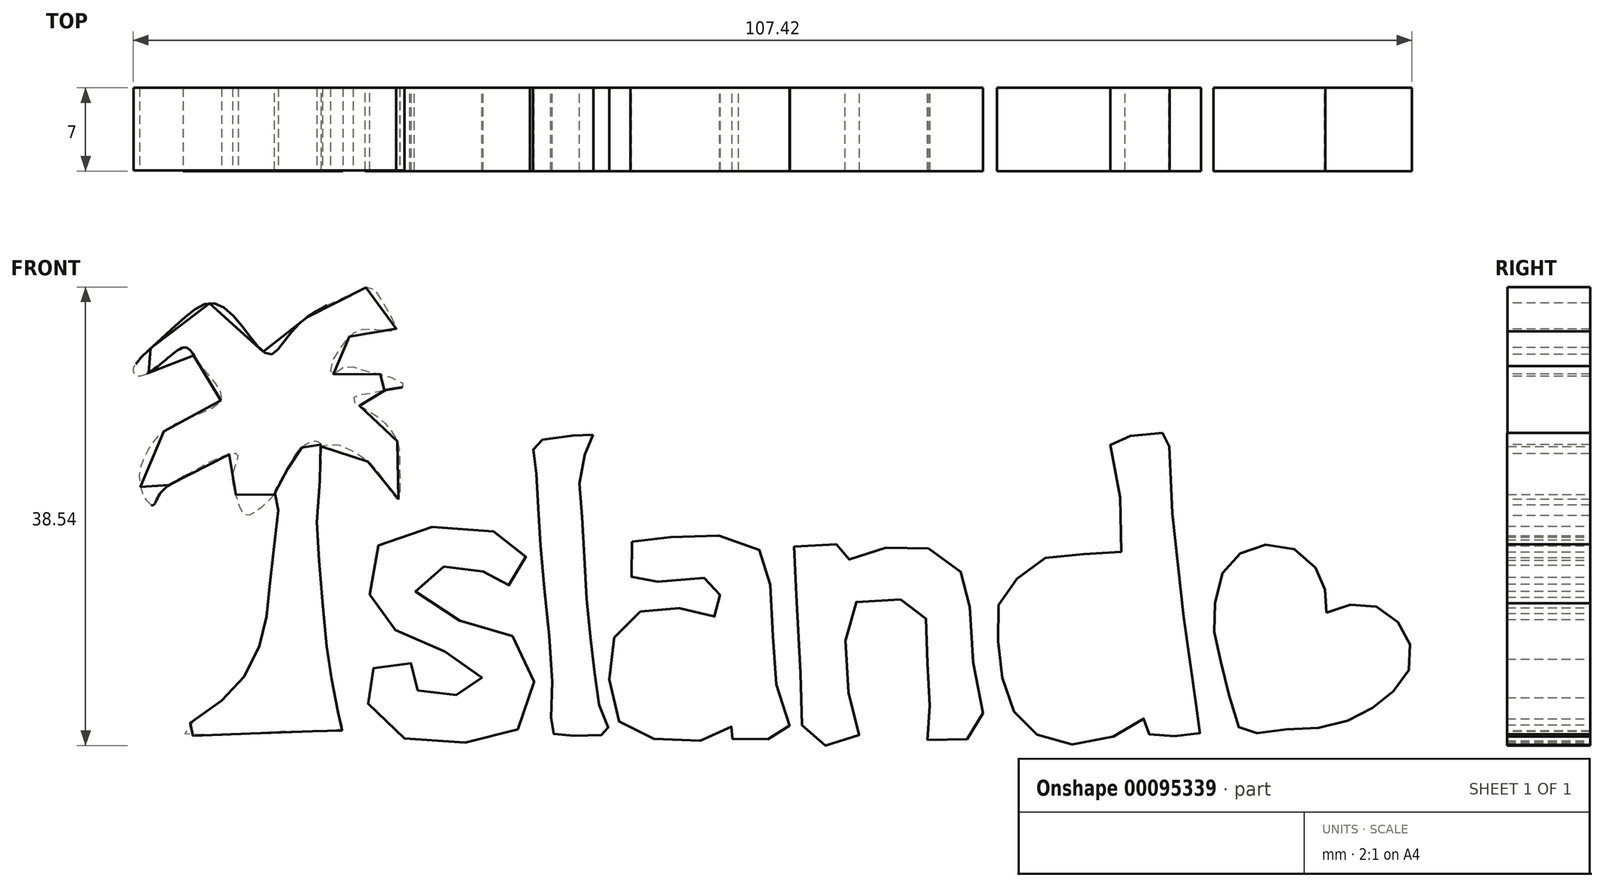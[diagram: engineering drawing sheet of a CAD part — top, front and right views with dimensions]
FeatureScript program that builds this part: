
annotation { "Feature Type Name" : "Feature", "Feature Type Description" : "" }
export const myFeature = defineFeature(function(context is Context, id is Id, definition is map)
    precondition{}
    {
        {
            var Q0;
            Q0=qCreatedBy(makeId("Front.planeOp"),FACE);
            var sketch = newSketch(context, id + "F0", { "sketchPlane" : qUnion([Q0])});
            skFitSpline(sketch, "E0", {"points": [v(-36.15, 19.95) * mm, v(-34.69, 20.39) * mm, v(-34.76, 16) * mm, v(-34.72, 10.92) * mm, v(-34.16, 4.35) * mm, v(-33.66, 0.5) * mm, v(-32.91, -2.96) * mm, v(-32.73, -3.8) * mm, v(-36.43, -3.89) * mm, v(-46.1, -4.03) * mm, v(-43.88, -2.08) * mm, v(-41.01, 0.65) * mm, v(-39.44, 4.16) * mm, v(-38.97, 6.94) * mm, v(-38.56, 11.06) * mm, v(-38.19, 15.4) * mm, v(-38.43, 16.02) * mm, v(-37.38, 18.07) * mm, v(-36.15, 19.95) * mm]});
            skFitSpline(sketch, "E1", {"points": [v(-26.39, -0.46) * mm, v(-26.94, 0) * mm, v(-27.04, 0.92) * mm, v(-27.04, 1.94) * mm, v(-28.24, 2.08) * mm, v(-30.23, 1.34) * mm, v(-30.7, 0.92) * mm, v(-30.74, -0.97) * mm, v(-29.4, -3.56) * mm, v(-26.94, -4.63) * mm, v(-23.1, -4.86) * mm, v(-19.3, -4.54) * mm, v(-17.6, -3.2) * mm, v(-16.72, -0.46) * mm, v(-16.76, 1.53) * mm, v(-18.52, 4.16) * mm, v(-21.53, 5.09) * mm, v(-24.35, 5.97) * mm, v(-26.57, 7.82) * mm, v(-26.2, 9.48) * mm, v(-23.9, 9.95) * mm, v(-21.3, 10.04) * mm, v(-20.93, 9.67) * mm, v(-20.88, 8.05) * mm, v(-18.85, 8.33) * mm, v(-17, 9.4) * mm, v(-17.27, 10.6) * mm, v(-17.74, 11.94) * mm, v(-20.05, 12.9) * mm, v(-23.8, 13.33) * mm, v(-27.78, 12.77) * mm, v(-29.95, 11.38) * mm, v(-30.32, 9.07) * mm, v(-30.28, 6.15) * mm, v(-28.7, 4.77) * mm, v(-26.34, 3.98) * mm, v(-23.38, 2.4) * mm, v(-21.44, 1.39) * mm, v(-20.93, 0) * mm, v(-21.25, -0.6) * mm, v(-23.61, -0.88) * mm, v(-25.74, -1.02) * mm, v(-26.39, -0.46) * mm]});
            skFitSpline(sketch, "E2", {"points": [v(-11.68, 21) * mm, v(-12.55, 18.88) * mm, v(-12.65, 14.67) * mm, v(-12.23, 7.4) * mm, v(-11.58, 1.34) * mm, v(-10.8, -2.82) * mm, v(-10.29, -3.98) * mm, v(-11.77, -4.26) * mm, v(-14.68, -4.21) * mm, v(-15.15, -3.93) * mm, v(-15.1, -0.6) * mm, v(-15.84, 8.74) * mm, v(-16.3, 15.55) * mm, v(-16.63, 19.48) * mm, v(-16.63, 20.31) * mm, v(-13.66, 20.91) * mm, v(-11.68, 21) * mm]});
            skFitSpline(sketch, "E3", {"points": [v(-8.39, 12.03) * mm, v(-8.44, 10.04) * mm, v(-8.3, 8.6) * mm, v(-6.72, 8.6) * mm, v(-3.2, 8.88) * mm, v(-1.13, 8.88) * mm, v(-1.03, 7.22) * mm, v(-1.08, 5.5) * mm, v(-2.1, 6.2) * mm, v(-4.46, 6.43) * mm, v(-6.96, 6.3) * mm, v(-9.04, 5.46) * mm, v(-10.15, 2.96) * mm, v(-10.29, 0) * mm, v(-9.55, -3) * mm, v(-7.46, -4.35) * mm, v(-4.46, -4.67) * mm, v(-1.08, -4.4) * mm, v(0, -3.47) * mm, v(0.54, -3.42) * mm, v(0, -4.4) * mm, v(1.14, -4.81) * mm, v(3.6, -4.4) * mm, v(4.7, -3.8) * mm, v(4.8, -3.24) * mm, v(3.73, 0) * mm, v(3.46, 3.84) * mm, v(3.22, 8.24) * mm, v(2.9, 10.55) * mm, v(0.96, 12.17) * mm, v(-2.6, 12.54) * mm, v(-6.35, 12.4) * mm, v(-8.39, 12.03) * mm]});
            skFitSpline(sketch, "E4", {"points": [v(5.21, 11.61) * mm, v(5.21, 8.8) * mm, v(5.77, 0) * mm, v(5.9, -3.56) * mm, v(6.6, -4.9) * mm, v(9.42, -4.9) * mm, v(10.67, -4.3) * mm, v(10.03, -1.9) * mm, v(9.6, 2.17) * mm, v(9.66, 5.7) * mm, v(10.95, 7.22) * mm, v(14.24, 7.17) * mm, v(15.8, 6.66) * mm, v(16.5, 4.07) * mm, v(16.41, 1.16) * mm, v(16.6, -1.62) * mm, v(16.55, -3.98) * mm, v(16.5, -4.72) * mm, v(19.23, -4.58) * mm, v(20.8, -4.26) * mm, v(20.95, -1.25) * mm, v(20.11, 2.78) * mm, v(19.93, 7.26) * mm, v(19.47, 9.02) * mm, v(18.17, 10.73) * mm, v(15.4, 11.66) * mm, v(12.7, 11.47) * mm, v(10.4, 10.73) * mm, v(9.33, 10.5) * mm, v(9.05, 11.15) * mm, v(8.45, 12.03) * mm, v(5.21, 11.61) * mm]});
            skFitSpline(sketch, "E5", {"points": [v(32.72, 11.17) * mm, v(31.8, 19.92) * mm, v(32.26, 20.71) * mm, v(35.42, 21.13) * mm, v(36.63, 21.09) * mm, v(36.73, 18.95) * mm, v(39.24, -2.97) * mm, v(39.33, -4.04) * mm, v(37.94, -4.28) * mm, v(35.42, -4.28) * mm, v(34.86, -3.86) * mm, v(34.68, -2.88) * mm, v(31.75, -4.51) * mm, v(27.1, -4.74) * mm, v(24.35, -3.16) * mm, v(22.86, 0) * mm, v(22.34, 3.87) * mm, v(22.62, 7.4) * mm, v(25, 9.73) * mm, v(28.2, 11.17) * mm, v(32.72, 11.17) * mm]});
            skFitSpline(sketch, "E6", {"points": [v(49.94, 6.05) * mm, v(51.76, 6.66) * mm, v(53.9, 6.66) * mm, v(55.71, 5.54) * mm, v(56.83, 3.87) * mm, v(57.06, 1.82) * mm, v(56.09, 0) * mm, v(54.55, -1.44) * mm, v(52.55, -2.65) * mm, v(50.04, -3.53) * mm, v(47.01, -3.72) * mm, v(44.22, -4.04) * mm, v(42.91, -4) * mm, v(41.94, -1.53) * mm, v(41, 2.2) * mm, v(40.5, 4.8) * mm, v(40.68, 7.45) * mm, v(41.57, 10.06) * mm, v(43.24, 11.31) * mm, v(45.43, 11.82) * mm, v(47.99, 10.99) * mm, v(49.38, 9.27) * mm, v(49.85, 7.64) * mm, v(49.94, 6.05) * mm]});
            skSolve(sketch);
        }
        {
            var Q0;
            Q0 = qSketchRegion(id + "F0", true);
            extrude(context, id + "F1", {"entities" : qUnion([Q0]), "depth" : 7 * mm});
        }
        {
            var Q0;
            Q0=qCreatedBy(makeId("Front.planeOp"),FACE);
            var sketch = newSketch(context, id + "F2", { "sketchPlane" : qUnion([Q0])});
            skFitSpline(sketch, "E7", {"points": [v(-34.52, 20.03) * mm, v(-36.18, 19.63) * mm, v(-37.04, 17.8) * mm, v(-38.36, 16.07) * mm, v(-40.77, 14.24) * mm, v(-41.52, 15.5) * mm, v(-41.92, 17.8) * mm, v(-41.52, 19.34) * mm, v(-43.3, 19) * mm, v(-46.22, 17.4) * mm, v(-48.06, 16.07) * mm, v(-48.69, 15.1) * mm, v(-49.66, 16.53) * mm, v(-49.43, 18.94) * mm, v(-47.77, 21.3) * mm, v(-45.02, 22.67) * mm, v(-42.9, 24.05) * mm, v(-43.64, 25.65) * mm, v(-45.02, 27.37) * mm, v(-45.88, 28.35) * mm, v(-47.71, 27.2) * mm, v(-49.9, 25.94) * mm, v(-50.3, 26.46) * mm, v(-49.32, 27.83) * mm, v(-46.5, 30.41) * mm, v(-43.58, 32.08) * mm, v(-40.66, 29.5) * mm, v(-38.76, 27.78) * mm, v(-37.1, 29.55) * mm, v(-34.58, 31.62) * mm, v(-31.53, 33.05) * mm, v(-30.27, 33.4) * mm, v(-29, 31.56) * mm, v(-28.26, 29.84) * mm, v(-30.5, 29.9) * mm, v(-31.82, 29.55) * mm, v(-32.85, 28.4) * mm, v(-33.71, 26.8) * mm, v(-33.6, 26.11) * mm, v(-32.57, 26.74) * mm, v(-31.02, 26.46) * mm, v(-28.72, 25.88) * mm, v(-27.52, 25.14) * mm, v(-28.38, 24.9) * mm, v(-30.62, 24.45) * mm, v(-31.7, 24.22) * mm, v(-31.82, 23.87) * mm, v(-30.04, 22.73) * mm, v(-28.72, 21.46) * mm, v(-28.03, 20.26) * mm, v(-27.92, 18.02) * mm, v(-28.03, 15.61) * mm, v(-28.72, 16.36) * mm, v(-29.81, 18.02) * mm, v(-31.48, 19.4) * mm, v(-33.37, 20.2) * mm, v(-34.52, 20.03) * mm]});
            skSolve(sketch);
        }
        {
            var Q0;
            Q0 = qSketchRegion(id + "F2", true);
            extrude(context, id + "F3", {"entities" : qUnion([Q0]), "operationType" : NewBodyOperationType.ADD, "depth" : 6.95 * mm});
        }
    });
